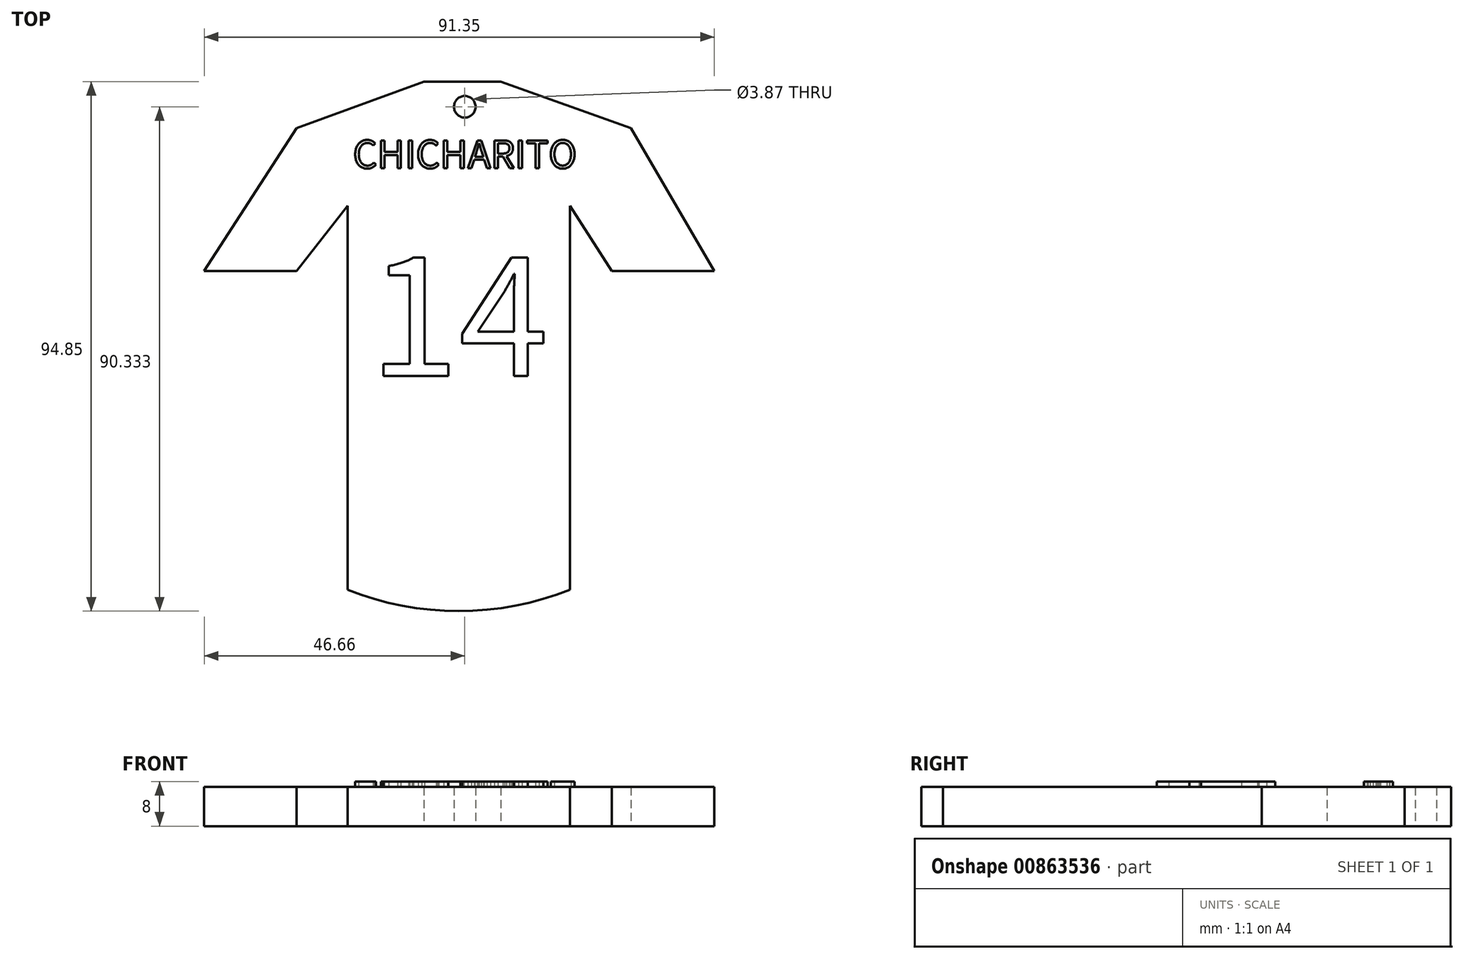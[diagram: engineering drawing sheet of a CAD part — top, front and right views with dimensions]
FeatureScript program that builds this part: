
annotation { "Feature Type Name" : "Feature", "Feature Type Description" : "" }
export const myFeature = defineFeature(function(context is Context, id is Id, definition is map)
    precondition{}
    {
        {
            var Q0;
            Q0=qCreatedBy(makeId("Top.planeOp"),FACE);
            var sketch = newSketch(context, id + "F0", { "sketchPlane" : qUnion([Q0])});
            skLineSegment(sketch, "E0", {"start": v(-21, -38.26) * mm, "end": v(-21, 30.5) * mm});
            skLineSegment(sketch, "E1", {"start": v(18.83, -38.26) * mm, "end": v(18.83, 30.5) * mm});
            skArc(sketch, "E2", {"start": v(-21, -38.26) * mm, "mid": v(-1.08, -42.1) * mm, "end": v(18.83, -38.26) * mm});
            skLineSegment(sketch, "E3", {"start": v(-7.33, 52.74) * mm, "end": v(6.47, 52.74) * mm});
            skLineSegment(sketch, "E4", {"start": v(6.47, 52.74) * mm, "end": v(29.75, 44.4) * mm});
            skLineSegment(sketch, "E5", {"start": v(29.75, 44.4) * mm, "end": v(44.7, 18.83) * mm});
            skLineSegment(sketch, "E6", {"start": v(44.7, 18.83) * mm, "end": v(26.3, 18.83) * mm});
            skLineSegment(sketch, "E7", {"start": v(26.3, 18.83) * mm, "end": v(18.83, 30.5) * mm});
            skPoint(sketch, "E8.start.orphan", {"position": v(-32.33, 18.83) * mm});
            skLineSegment(sketch, "E9", {"start": v(-30.1, 18.83) * mm, "end": v(-46.66, 18.83) * mm});
            skLineSegment(sketch, "E10", {"start": v(-30.1, 18.83) * mm, "end": v(-21, 30.5) * mm});
            skPoint(sketch, "E11.end.orphan", {"position": v(-30.1, 45.64) * mm});
            skPoint(sketch, "E11.start.orphan", {"position": v(26.3, 45.64) * mm});
            skLineSegment(sketch, "E12", {"start": v(-7.33, 52.74) * mm, "end": v(-30.1, 44.4) * mm});
            skLineSegment(sketch, "E13", {"start": v(-30.1, 44.4) * mm, "end": v(-46.66, 18.83) * mm});
            skPoint(sketch, "E14.end.orphan", {"position": v(-34.06, 44.4) * mm});
            skPoint(sketch, "E15.orphan", {"position": v(-48.43, 18.83) * mm});
            skSolve(sketch);
        }
        {
            var Q0;
            Q0 = qSketchRegion(id + "F0", true);
            extrude(context, id + "F1", {"entities" : qUnion([Q0]), "depth" : 7 * mm, "offsetDistance" : 25 * mm});
        }
        {
            var Q0;
            Q0=qCreatedBy(makeId("Top.planeOp"),FACE);
            var sketch = newSketch(context, id + "F2", { "sketchPlane" : qUnion([Q0])});
            skText(sketch, "E16", { "text": "CHICHARITO", "fontName": "NotoSansCJKsc-Regular.otf"});
            const initialGuessF2  = {"E16": [-0.02002, 0.03722, 1, 0, 0.00489]};
            skSetInitialGuess(sketch, initialGuessF2);
            skSolve(sketch);
        }
        {
            var Q0;
            Q0 = qSketchRegion(id + "F2", true);
            extrude(context, id + "F3", {"entities" : qUnion([Q0]), "operationType" : NewBodyOperationType.ADD, "depth" : 8 * mm, "offsetDistance" : 25 * mm});
        }
        {
            var Q0;
            Q0=qCreatedBy(makeId("Top.planeOp"),FACE);
            var sketch = newSketch(context, id + "F4", { "sketchPlane" : qUnion([Q0])});
            skText(sketch, "E17", { "text": "14", "fontName": "NotoSansCJKsc-Regular.otf"});
            const initialGuessF4  = {"E17": [-0.0171, 0, 1, 0, 0.02084]};
            skSetInitialGuess(sketch, initialGuessF4);
            skSolve(sketch);
        }
        {
            var Q0;
            Q0 = qSketchRegion(id + "F4", true);
            extrude(context, id + "F5", {"entities" : qUnion([Q0]), "operationType" : NewBodyOperationType.ADD, "depth" : 8 * mm, "offsetDistance" : 25 * mm});
        }
        {
            var Q0;
            Q0=qCreatedBy(makeId("Top.planeOp"),FACE);
            var sketch = newSketch(context, id + "F6", { "sketchPlane" : qUnion([Q0])});
            skCircle(sketch, "E18", {"center": v(0, 48.22) * mm, "radius": 1.93 * mm});
            skSolve(sketch);
        }
        {
            var Q0;
            Q0 = qSketchRegion(id + "F6", true);
            extrude(context, id + "F7", {"entities" : qUnion([Q0]), "operationType" : NewBodyOperationType.REMOVE, "oppositeDirection" : true, "depth" : 25 * mm, "offsetDistance" : 25 * mm});
        }
        {
            var Q0;
            Q0 = qSketchRegion(id + "F6", true);
            extrude(context, id + "F8", {"entities" : qUnion([Q0]), "operationType" : NewBodyOperationType.REMOVE, "depth" : 27.3 * mm, "offsetDistance" : 25 * mm});
        }
    });
